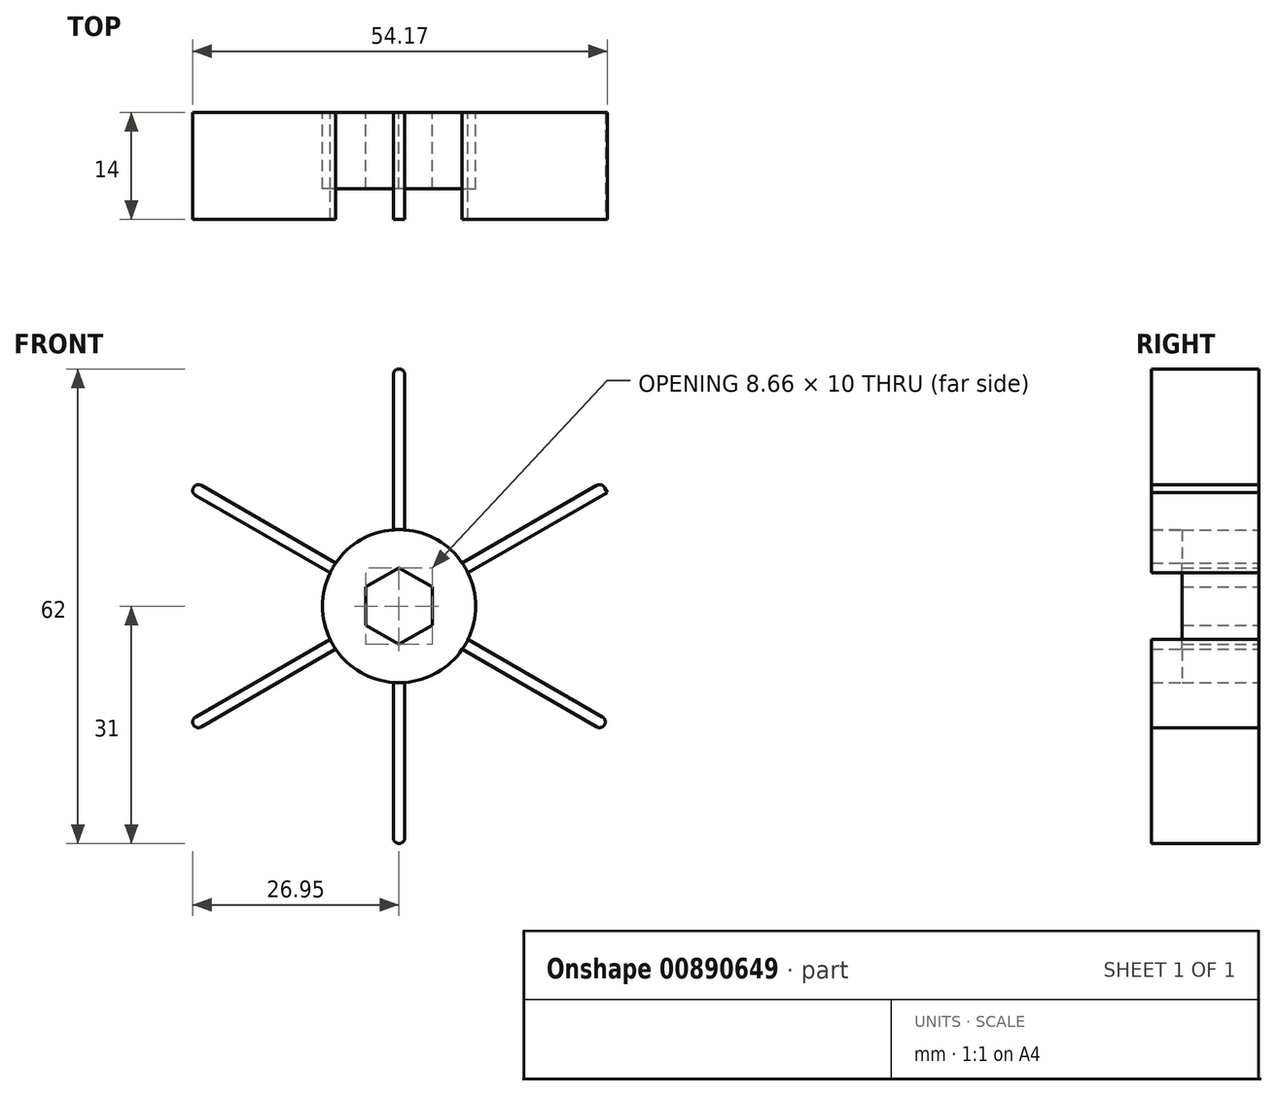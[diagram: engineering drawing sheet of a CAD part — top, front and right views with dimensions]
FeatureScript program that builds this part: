
annotation { "Feature Type Name" : "Feature", "Feature Type Description" : "" }
export const myFeature = defineFeature(function(context is Context, id is Id, definition is map)
    precondition{}
    {
        {
            var Q0;
            Q0=qCreatedBy(makeId("Front.planeOp"),FACE);
            var sketch = newSketch(context, id + "F0", { "sketchPlane" : qUnion([Q0])});
            skCircle(sketch, "E0", {"center": v(0, 0) * mm, "radius": 10 * mm});
            skCircle(sketch, "E1", {"center": v(0, 0) * mm, "radius": 5 * mm});
            skCircle(sketch, "E2.cCircle", {"center": v(0, 0) * mm, "radius": 5 * mm, "construction": true});
            skLineSegment(sketch, "E2.0", {"start": v(0, 5) * mm, "end": v(4.33, 2.5) * mm});
            skLineSegment(sketch, "E2.1", {"start": v(4.33, 2.5) * mm, "end": v(4.33, -2.5) * mm});
            skLineSegment(sketch, "E2.2", {"start": v(4.33, -2.5) * mm, "end": v(0, -5) * mm});
            skLineSegment(sketch, "E2.3", {"start": v(0, -5) * mm, "end": v(-4.33, -2.5) * mm});
            skLineSegment(sketch, "E2.4", {"start": v(-4.33, -2.5) * mm, "end": v(-4.33, 2.5) * mm});
            skLineSegment(sketch, "E2.5", {"start": v(-4.33, 2.5) * mm, "end": v(0, 5) * mm});
            skLineSegment(sketch, "E3", {"start": v(-0.75, 31) * mm, "end": v(0.75, 31) * mm});
            skLineSegment(sketch, "E4", {"start": v(0.75, 31) * mm, "end": v(0.75, 0) * mm});
            skLineSegment(sketch, "E5", {"start": v(-0.75, 31) * mm, "end": v(-0.75, 0) * mm});
            skLineSegment(sketch, "E6.1.0", {"start": v(-26.47, 16.15) * mm, "end": v(0.38, 0.65) * mm});
            skLineSegment(sketch, "E6.1.1", {"start": v(-27.22, 14.85) * mm, "end": v(-0.38, -0.65) * mm});
            skLineSegment(sketch, "E6.1.2", {"start": v(-27.22, 14.85) * mm, "end": v(-26.47, 16.15) * mm});
            skLineSegment(sketch, "E6.2.0", {"start": v(-27.22, -14.85) * mm, "end": v(-0.37, 0.65) * mm});
            skLineSegment(sketch, "E6.2.1", {"start": v(-26.47, -16.15) * mm, "end": v(0.38, -0.65) * mm});
            skLineSegment(sketch, "E6.2.2", {"start": v(-26.47, -16.15) * mm, "end": v(-27.22, -14.85) * mm});
            skLineSegment(sketch, "E6.3.0", {"start": v(-0.75, -31) * mm, "end": v(-0.75, 0) * mm});
            skLineSegment(sketch, "E6.3.1", {"start": v(0.75, -31) * mm, "end": v(0.75, 0) * mm});
            skLineSegment(sketch, "E6.3.2", {"start": v(0.75, -31) * mm, "end": v(-0.75, -31) * mm});
            skLineSegment(sketch, "E6.4.0", {"start": v(26.47, -16.15) * mm, "end": v(-0.38, -0.65) * mm});
            skLineSegment(sketch, "E6.4.1", {"start": v(27.22, -14.85) * mm, "end": v(0.38, 0.65) * mm});
            skLineSegment(sketch, "E6.4.2", {"start": v(27.22, -14.85) * mm, "end": v(26.47, -16.15) * mm});
            skLineSegment(sketch, "E6.5.0", {"start": v(27.22, 14.85) * mm, "end": v(0.38, -0.65) * mm});
            skLineSegment(sketch, "E6.5.1", {"start": v(26.47, 16.15) * mm, "end": v(-0.38, 0.65) * mm});
            skLineSegment(sketch, "E6.5.2", {"start": v(26.47, 16.15) * mm, "end": v(27.22, 14.85) * mm});
            skSolve(sketch);
        }
        {
            var Q0;
            {var subQ0=sQuery(id+"F0.wireOp",EDGE,"819567e6-a781-46ed-af89-72056181dca4.4.0");var subQ1=makeQuery(id+"F0.imprint","IMPRINT",VERTEX,{"derivedFrom":subQ0});Q0=makeQuery(id+"F0.imprint","IMPRINT",FACE,{"disambiguationData":[TD([[makeQuery(id+"F0.imprint","IMPRINT",EDGE,{"disambiguationData":[TD([[subQ1,1.0]])],"derivedFrom":subQ0}),1.0]])]});}
            var Q1;
            {var subQ2=sQuery(id+"F0.wireOp",EDGE,"819567e6-a781-46ed-af89-72056181dca4.5.0");var subQ4=makeQuery(id+"F0.imprint","IMPRINT",VERTEX,{"derivedFrom":subQ2});Q1=makeQuery(id+"F0.imprint","IMPRINT",FACE,{"disambiguationData":[TD([[makeQuery(id+"F0.imprint","IMPRINT",EDGE,{"disambiguationData":[TD([[subQ4,1.0]])],"derivedFrom":subQ2}),-1.0]])]});}
            var Q2;
            {var subQ5=sQuery(id+"F0.wireOp",EDGE,"819567e6-a781-46ed-af89-72056181dca4.5.0");var subQ6=makeQuery(id+"F0.imprint","IMPRINT",VERTEX,{"derivedFrom":subQ5});Q2=makeQuery(id+"F0.imprint","IMPRINT",FACE,{"disambiguationData":[TD([[makeQuery(id+"F0.imprint","IMPRINT",EDGE,{"disambiguationData":[TD([[subQ6,1.0]])],"derivedFrom":subQ5}),1.0]])]});}
            var Q3;
            {var subQ3=sQuery(id+"F0.wireOp",EDGE,"E0");var subQ10=sQuery(id+"F0.wireOp",EDGE,"98a826cf-b40a-42a3-8d70-f6cf4cde65dd2.MirrorCS");var subQ11=makeQuery(id+"F0.imprint","INTERSECT",VERTEX,{"derivedFrom":[subQ3,subQ10]});Q3=makeQuery(id+"F0.imprint","IMPRINT",FACE,{"disambiguationData":[TD([[makeQuery(id+"F0.imprint","IMPRINT",EDGE,{"disambiguationData":[TD([[subQ11,-1.0]])],"derivedFrom":subQ3}),1.0]])]});}
            var Q4;
            {var subQ3=sQuery(id+"F0.wireOp",EDGE,"E0");var subQ9=sQuery(id+"F0.wireOp",EDGE,"s4JnZFQR-gPvF-xN2i-koIt-LSXhCspGUzUX");var subQ11=makeQuery(id+"F0.imprint","INTERSECT",VERTEX,{"derivedFrom":[subQ3,subQ9]});Q4=makeQuery(id+"F0.imprint","IMPRINT",FACE,{"disambiguationData":[TD([[makeQuery(id+"F0.imprint","IMPRINT",EDGE,{"disambiguationData":[TD([[subQ11,-1.0]])],"derivedFrom":subQ3}),1.0]])]});}
            var Q5;
            {var subQ3=sQuery(id+"F0.wireOp",EDGE,"E0");var subQ6=sQuery(id+"F0.wireOp",EDGE,"819567e6-a781-46ed-af89-72056181dca4.1.2");var subQ12=makeQuery(id+"F0.imprint","INTERSECT",VERTEX,{"derivedFrom":[subQ3,subQ6]});Q5=makeQuery(id+"F0.imprint","IMPRINT",FACE,{"disambiguationData":[TD([[makeQuery(id+"F0.imprint","IMPRINT",EDGE,{"disambiguationData":[TD([[subQ12,-1.0]])],"derivedFrom":subQ3}),1.0]])]});}
            var Q6;
            {var subQ3=sQuery(id+"F0.wireOp",EDGE,"E0");var subQ6=sQuery(id+"F0.wireOp",EDGE,"819567e6-a781-46ed-af89-72056181dca4.1.0");var subQ8=makeQuery(id+"F0.imprint","INTERSECT",VERTEX,{"derivedFrom":[subQ3,subQ6]});Q6=makeQuery(id+"F0.imprint","IMPRINT",FACE,{"disambiguationData":[TD([[makeQuery(id+"F0.imprint","IMPRINT",EDGE,{"disambiguationData":[TD([[subQ8,-1.0]])],"derivedFrom":subQ3}),1.0]])]});}
            var Q7;
            {var subQ3=sQuery(id+"F0.wireOp",EDGE,"E0");var subQ10=sQuery(id+"F0.wireOp",EDGE,"819567e6-a781-46ed-af89-72056181dca4.2.2");var subQ12=makeQuery(id+"F0.imprint","INTERSECT",VERTEX,{"derivedFrom":[subQ3,subQ10]});Q7=makeQuery(id+"F0.imprint","IMPRINT",FACE,{"disambiguationData":[TD([[makeQuery(id+"F0.imprint","IMPRINT",EDGE,{"disambiguationData":[TD([[subQ12,-1.0]])],"derivedFrom":subQ3}),1.0]])]});}
            var Q8;
            {var subQ0=sQuery(id+"F0.wireOp",EDGE,"819567e6-a781-46ed-af89-72056181dca4.3.2");var subQ1=makeQuery(id+"F0.imprint","IMPRINT",VERTEX,{"derivedFrom":subQ0});Q8=makeQuery(id+"F0.imprint","IMPRINT",FACE,{"disambiguationData":[TD([[makeQuery(id+"F0.imprint","IMPRINT",EDGE,{"disambiguationData":[TD([[subQ1,1.0]])],"derivedFrom":subQ0}),-1.0]])]});}
            var Q9;
            {var subQ0=sQuery(id+"F0.wireOp",EDGE,"819567e6-a781-46ed-af89-72056181dca4.3.0");var subQ1=makeQuery(id+"F0.imprint","IMPRINT",VERTEX,{"derivedFrom":subQ0});Q9=makeQuery(id+"F0.imprint","IMPRINT",FACE,{"disambiguationData":[TD([[makeQuery(id+"F0.imprint","IMPRINT",EDGE,{"disambiguationData":[TD([[subQ1,1.0]])],"derivedFrom":subQ0}),-1.0]])]});}
            var Q10;
            {var subQ0=sQuery(id+"F0.wireOp",EDGE,"819567e6-a781-46ed-af89-72056181dca4.3.0");var subQ1=makeQuery(id+"F0.imprint","IMPRINT",VERTEX,{"derivedFrom":subQ0});Q10=makeQuery(id+"F0.imprint","IMPRINT",FACE,{"disambiguationData":[TD([[makeQuery(id+"F0.imprint","IMPRINT",EDGE,{"disambiguationData":[TD([[subQ1,1.0]])],"derivedFrom":subQ0}),1.0]])]});}
            var Q11;
            {var subQ0=sQuery(id+"F0.wireOp",EDGE,"819567e6-a781-46ed-af89-72056181dca4.4.0");var subQ1=makeQuery(id+"F0.imprint","IMPRINT",VERTEX,{"derivedFrom":subQ0});Q11=makeQuery(id+"F0.imprint","IMPRINT",FACE,{"disambiguationData":[TD([[makeQuery(id+"F0.imprint","IMPRINT",EDGE,{"disambiguationData":[TD([[subQ1,1.0]])],"derivedFrom":subQ0}),-1.0]])]});}
            var Q12;
            {var subQ0=sQuery(id+"F0.wireOp",EDGE,"819567e6-a781-46ed-af89-72056181dca4.5.2");var subQ1=sQuery(id+"F0.wireOp",EDGE,"E1");var subQ2=makeQuery(id+"F0.imprint","INTERSECT",VERTEX,{"disambiguationData":[OD(0.0)],"derivedFrom":[subQ1,subQ0]});Q12=makeQuery(id+"F0.imprint","IMPRINT",FACE,{"disambiguationData":[TD([[makeQuery(id+"F0.imprint","IMPRINT",EDGE,{"disambiguationData":[TD([[subQ2,1.0]])],"derivedFrom":subQ1}),1.0]])]});}
            var Q13;
            {var subQ1=sQuery(id+"F0.wireOp",EDGE,"E1");var subQ3=sQuery(id+"F0.wireOp",EDGE,"819567e6-a781-46ed-af89-72056181dca4.5.2");var subQ4=makeQuery(id+"F0.imprint","INTERSECT",VERTEX,{"disambiguationData":[OD(0.0)],"derivedFrom":[subQ1,subQ3]});Q13=makeQuery(id+"F0.imprint","IMPRINT",FACE,{"disambiguationData":[TD([[makeQuery(id+"F0.imprint","IMPRINT",EDGE,{"disambiguationData":[TD([[subQ4,1.0]])],"derivedFrom":subQ3}),1.0]])]});}
            var Q14;
            {var subQ1=sQuery(id+"F0.wireOp",EDGE,"E1");var subQ3=sQuery(id+"F0.wireOp",EDGE,"819567e6-a781-46ed-af89-72056181dca4.4.0");var subQ4=makeQuery(id+"F0.imprint","INTERSECT",VERTEX,{"disambiguationData":[OD(1.0)],"derivedFrom":[subQ1,subQ3]});Q14=makeQuery(id+"F0.imprint","IMPRINT",FACE,{"disambiguationData":[TD([[makeQuery(id+"F0.imprint","IMPRINT",EDGE,{"disambiguationData":[TD([[subQ4,1.0]])],"derivedFrom":subQ3}),-1.0]])]});}
            var Q15;
            {var subQ1=sQuery(id+"F0.wireOp",EDGE,"E1");var subQ3=sQuery(id+"F0.wireOp",EDGE,"819567e6-a781-46ed-af89-72056181dca4.4.2");var subQ4=makeQuery(id+"F0.imprint","INTERSECT",VERTEX,{"disambiguationData":[OD(1.0)],"derivedFrom":[subQ1,subQ3]});Q15=makeQuery(id+"F0.imprint","IMPRINT",FACE,{"disambiguationData":[TD([[makeQuery(id+"F0.imprint","IMPRINT",EDGE,{"disambiguationData":[TD([[subQ4,1.0]])],"derivedFrom":subQ3}),1.0]])]});}
            var Q16;
            {var subQ0=sQuery(id+"F0.wireOp",EDGE,"819567e6-a781-46ed-af89-72056181dca4.3.0");var subQ1=sQuery(id+"F0.wireOp",EDGE,"E1");var subQ2=makeQuery(id+"F0.imprint","INTERSECT",VERTEX,{"disambiguationData":[OD(1.0)],"derivedFrom":[subQ1,subQ0]});Q16=makeQuery(id+"F0.imprint","IMPRINT",FACE,{"disambiguationData":[TD([[makeQuery(id+"F0.imprint","IMPRINT",EDGE,{"disambiguationData":[TD([[subQ2,-1.0]])],"derivedFrom":subQ1}),1.0]])]});}
            var Q17;
            {var subQ1=sQuery(id+"F0.wireOp",EDGE,"E1");var subQ3=sQuery(id+"F0.wireOp",EDGE,"819567e6-a781-46ed-af89-72056181dca4.3.0");var subQ4=makeQuery(id+"F0.imprint","INTERSECT",VERTEX,{"disambiguationData":[OD(1.0)],"derivedFrom":[subQ1,subQ3]});Q17=makeQuery(id+"F0.imprint","IMPRINT",FACE,{"disambiguationData":[TD([[makeQuery(id+"F0.imprint","IMPRINT",EDGE,{"disambiguationData":[TD([[subQ4,1.0]])],"derivedFrom":subQ3}),-1.0]])]});}
            var Q18;
            {var subQ0=sQuery(id+"F0.wireOp",EDGE,"819567e6-a781-46ed-af89-72056181dca4.5.2");var subQ1=sQuery(id+"F0.wireOp",EDGE,"E1");var subQ2=makeQuery(id+"F0.imprint","INTERSECT",VERTEX,{"disambiguationData":[OD(1.0)],"derivedFrom":[subQ1,subQ0]});Q18=makeQuery(id+"F0.imprint","IMPRINT",FACE,{"disambiguationData":[TD([[makeQuery(id+"F0.imprint","IMPRINT",EDGE,{"disambiguationData":[TD([[subQ2,-1.0]])],"derivedFrom":subQ1}),1.0]])]});}
            var Q19;
            {var subQ1=sQuery(id+"F0.wireOp",EDGE,"E1");var subQ3=sQuery(id+"F0.wireOp",EDGE,"819567e6-a781-46ed-af89-72056181dca4.3.2");var subQ4=makeQuery(id+"F0.imprint","INTERSECT",VERTEX,{"disambiguationData":[OD(1.0)],"derivedFrom":[subQ1,subQ3]});Q19=makeQuery(id+"F0.imprint","IMPRINT",FACE,{"disambiguationData":[TD([[makeQuery(id+"F0.imprint","IMPRINT",EDGE,{"disambiguationData":[TD([[subQ4,1.0]])],"derivedFrom":subQ3}),1.0]])]});}
            var Q20;
            {var subQ1=sQuery(id+"F0.wireOp",EDGE,"E1");var subQ3=sQuery(id+"F0.wireOp",EDGE,"819567e6-a781-46ed-af89-72056181dca4.5.2");var subQ4=makeQuery(id+"F0.imprint","INTERSECT",VERTEX,{"disambiguationData":[OD(1.0)],"derivedFrom":[subQ1,subQ3]});Q20=makeQuery(id+"F0.imprint","IMPRINT",FACE,{"disambiguationData":[TD([[makeQuery(id+"F0.imprint","IMPRINT",EDGE,{"disambiguationData":[TD([[subQ4,-1.0]])],"derivedFrom":subQ3}),1.0]])]});}
            var Q21;
            {var subQ0=sQuery(id+"F0.wireOp",EDGE,"819567e6-a781-46ed-af89-72056181dca4.4.2");var subQ1=sQuery(id+"F0.wireOp",EDGE,"E1");var subQ2=makeQuery(id+"F0.imprint","INTERSECT",VERTEX,{"disambiguationData":[OD(0.0)],"derivedFrom":[subQ1,subQ0]});Q21=makeQuery(id+"F0.imprint","IMPRINT",FACE,{"disambiguationData":[TD([[makeQuery(id+"F0.imprint","IMPRINT",EDGE,{"disambiguationData":[TD([[subQ2,-1.0]])],"derivedFrom":subQ1}),1.0]])]});}
            var Q22;
            {var subQ1=sQuery(id+"F0.wireOp",EDGE,"E1");var subQ3=sQuery(id+"F0.wireOp",EDGE,"819567e6-a781-46ed-af89-72056181dca4.5.0");var subQ4=makeQuery(id+"F0.imprint","INTERSECT",VERTEX,{"disambiguationData":[OD(1.0)],"derivedFrom":[subQ1,subQ3]});Q22=makeQuery(id+"F0.imprint","IMPRINT",FACE,{"disambiguationData":[TD([[makeQuery(id+"F0.imprint","IMPRINT",EDGE,{"disambiguationData":[TD([[subQ4,-1.0]])],"derivedFrom":subQ3}),-1.0]])]});}
            var Q23;
            {var subQ1=sQuery(id+"F0.wireOp",EDGE,"E1");var subQ3=sQuery(id+"F0.wireOp",EDGE,"819567e6-a781-46ed-af89-72056181dca4.4.2");var subQ4=makeQuery(id+"F0.imprint","INTERSECT",VERTEX,{"disambiguationData":[OD(0.0)],"derivedFrom":[subQ1,subQ3]});Q23=makeQuery(id+"F0.imprint","IMPRINT",FACE,{"disambiguationData":[TD([[makeQuery(id+"F0.imprint","IMPRINT",EDGE,{"disambiguationData":[TD([[subQ4,-1.0]])],"derivedFrom":subQ3}),1.0]])]});}
            var Q24;
            {var subQ1=sQuery(id+"F0.wireOp",EDGE,"E1");var subQ3=sQuery(id+"F0.wireOp",EDGE,"819567e6-a781-46ed-af89-72056181dca4.4.0");var subQ4=makeQuery(id+"F0.imprint","INTERSECT",VERTEX,{"disambiguationData":[OD(0.0)],"derivedFrom":[subQ1,subQ3]});Q24=makeQuery(id+"F0.imprint","IMPRINT",FACE,{"disambiguationData":[TD([[makeQuery(id+"F0.imprint","IMPRINT",EDGE,{"disambiguationData":[TD([[subQ4,-1.0]])],"derivedFrom":subQ3}),-1.0]])]});}
            var Q25;
            {var subQ0=sQuery(id+"F0.wireOp",EDGE,"819567e6-a781-46ed-af89-72056181dca4.3.2");var subQ1=sQuery(id+"F0.wireOp",EDGE,"E1");var subQ2=makeQuery(id+"F0.imprint","INTERSECT",VERTEX,{"disambiguationData":[OD(0.0)],"derivedFrom":[subQ1,subQ0]});Q25=makeQuery(id+"F0.imprint","IMPRINT",FACE,{"disambiguationData":[TD([[makeQuery(id+"F0.imprint","IMPRINT",EDGE,{"disambiguationData":[TD([[subQ2,-1.0]])],"derivedFrom":subQ1}),1.0]])]});}
            var Q26;
            {var subQ1=sQuery(id+"F0.wireOp",EDGE,"E1");var subQ3=sQuery(id+"F0.wireOp",EDGE,"819567e6-a781-46ed-af89-72056181dca4.3.2");var subQ4=makeQuery(id+"F0.imprint","INTERSECT",VERTEX,{"disambiguationData":[OD(0.0)],"derivedFrom":[subQ1,subQ3]});Q26=makeQuery(id+"F0.imprint","IMPRINT",FACE,{"disambiguationData":[TD([[makeQuery(id+"F0.imprint","IMPRINT",EDGE,{"disambiguationData":[TD([[subQ4,-1.0]])],"derivedFrom":subQ3}),1.0]])]});}
            var Q27;
            {var subQ1=sQuery(id+"F0.wireOp",EDGE,"E1");var subQ3=sQuery(id+"F0.wireOp",EDGE,"819567e6-a781-46ed-af89-72056181dca4.3.0");var subQ4=makeQuery(id+"F0.imprint","INTERSECT",VERTEX,{"disambiguationData":[OD(0.0)],"derivedFrom":[subQ1,subQ3]});Q27=makeQuery(id+"F0.imprint","IMPRINT",FACE,{"disambiguationData":[TD([[makeQuery(id+"F0.imprint","IMPRINT",EDGE,{"disambiguationData":[TD([[subQ4,-1.0]])],"derivedFrom":subQ3}),-1.0]])]});}
            var Q28;
            {var subQ0=sQuery(id+"F0.wireOp",EDGE,"819567e6-a781-46ed-af89-72056181dca4.5.0");var subQ1=sQuery(id+"F0.wireOp",EDGE,"E1");var subQ2=makeQuery(id+"F0.imprint","INTERSECT",VERTEX,{"disambiguationData":[OD(0.0)],"derivedFrom":[subQ1,subQ0]});Q28=makeQuery(id+"F0.imprint","IMPRINT",FACE,{"disambiguationData":[TD([[makeQuery(id+"F0.imprint","IMPRINT",EDGE,{"disambiguationData":[TD([[subQ2,-1.0]])],"derivedFrom":subQ1}),1.0]])]});}
            var Q29;
            {var subQ1=sQuery(id+"F0.wireOp",EDGE,"E1");var subQ3=sQuery(id+"F0.wireOp",EDGE,"819567e6-a781-46ed-af89-72056181dca4.5.0");var subQ4=makeQuery(id+"F0.imprint","INTERSECT",VERTEX,{"disambiguationData":[OD(0.0)],"derivedFrom":[subQ1,subQ3]});Q29=makeQuery(id+"F0.imprint","IMPRINT",FACE,{"disambiguationData":[TD([[makeQuery(id+"F0.imprint","IMPRINT",EDGE,{"disambiguationData":[TD([[subQ4,1.0]])],"derivedFrom":subQ3}),-1.0]])]});}
            var Q30;
            {var subQ1=sQuery(id+"F0.wireOp",EDGE,"E0");var subQ6=sQuery(id+"F0.wireOp",EDGE,"E6.5.1");var subQ8=makeQuery(id+"F0.imprint","INTERSECT",VERTEX,{"derivedFrom":[subQ1,subQ6]});Q30=makeQuery(id+"F0.imprint","IMPRINT",FACE,{"disambiguationData":[TD([[makeQuery(id+"F0.imprint","IMPRINT",EDGE,{"disambiguationData":[TD([[subQ8,1.0]])],"derivedFrom":subQ1}),1.0]])]});}
            var Q31;
            {var subQ4=sQuery(id+"F0.wireOp",EDGE,"E4");var subQ5=sQuery(id+"F0.wireOp",EDGE,"E0");var subQ6=makeQuery(id+"F0.imprint","INTERSECT",VERTEX,{"derivedFrom":[subQ5,subQ4]});Q31=makeQuery(id+"F0.imprint","IMPRINT",FACE,{"disambiguationData":[TD([[makeQuery(id+"F0.imprint","IMPRINT",EDGE,{"disambiguationData":[TD([[subQ6,-1.0]])],"derivedFrom":subQ5}),1.0]])]});}
            var Q32;
            {var subQ0=sQuery(id+"F0.wireOp",EDGE,"E6.1.0");var subQ1=sQuery(id+"F0.wireOp",EDGE,"E0");var subQ2=makeQuery(id+"F0.imprint","INTERSECT",VERTEX,{"derivedFrom":[subQ1,subQ0]});Q32=makeQuery(id+"F0.imprint","IMPRINT",FACE,{"disambiguationData":[TD([[makeQuery(id+"F0.imprint","IMPRINT",EDGE,{"disambiguationData":[TD([[subQ2,-1.0]])],"derivedFrom":subQ1}),1.0]])]});}
            var Q33;
            {var subQ0=sQuery(id+"F0.wireOp",EDGE,"E6.2.0");var subQ1=sQuery(id+"F0.wireOp",EDGE,"E0");var subQ2=makeQuery(id+"F0.imprint","INTERSECT",VERTEX,{"derivedFrom":[subQ1,subQ0]});Q33=makeQuery(id+"F0.imprint","IMPRINT",FACE,{"disambiguationData":[TD([[makeQuery(id+"F0.imprint","IMPRINT",EDGE,{"disambiguationData":[TD([[subQ2,-1.0]])],"derivedFrom":subQ1}),1.0]])]});}
            var Q34;
            {var subQ4=sQuery(id+"F0.wireOp",EDGE,"E6.3.0");var subQ6=sQuery(id+"F0.wireOp",EDGE,"E0");var subQ7=makeQuery(id+"F0.imprint","INTERSECT",VERTEX,{"derivedFrom":[subQ6,subQ4]});Q34=makeQuery(id+"F0.imprint","IMPRINT",FACE,{"disambiguationData":[TD([[makeQuery(id+"F0.imprint","IMPRINT",EDGE,{"disambiguationData":[TD([[subQ7,-1.0]])],"derivedFrom":subQ6}),1.0]])]});}
            var Q35;
            {var subQ0=sQuery(id+"F0.wireOp",EDGE,"E6.4.0");var subQ1=sQuery(id+"F0.wireOp",EDGE,"E0");var subQ2=makeQuery(id+"F0.imprint","INTERSECT",VERTEX,{"derivedFrom":[subQ1,subQ0]});Q35=makeQuery(id+"F0.imprint","IMPRINT",FACE,{"disambiguationData":[TD([[makeQuery(id+"F0.imprint","IMPRINT",EDGE,{"disambiguationData":[TD([[subQ2,-1.0]])],"derivedFrom":subQ1}),1.0]])]});}
            var Q36;
            {var subQ0=sQuery(id+"F0.wireOp",EDGE,"E6.5.1");var subQ1=sQuery(id+"F0.wireOp",EDGE,"E1");var subQ2=makeQuery(id+"F0.imprint","INTERSECT",VERTEX,{"derivedFrom":[subQ1,subQ0]});Q36=makeQuery(id+"F0.imprint","IMPRINT",FACE,{"disambiguationData":[TD([[makeQuery(id+"F0.imprint","IMPRINT",EDGE,{"disambiguationData":[TD([[subQ2,-1.0]])],"derivedFrom":subQ1}),1.0]])]});}
            var Q37;
            {var subQ0=sQuery(id+"F0.wireOp",EDGE,"E6.5.0");var subQ1=sQuery(id+"F0.wireOp",EDGE,"E1");var subQ2=makeQuery(id+"F0.imprint","INTERSECT",VERTEX,{"derivedFrom":[subQ1,subQ0]});Q37=makeQuery(id+"F0.imprint","IMPRINT",FACE,{"disambiguationData":[TD([[makeQuery(id+"F0.imprint","IMPRINT",EDGE,{"disambiguationData":[TD([[subQ2,1.0]])],"derivedFrom":subQ1}),1.0]])]});}
            var Q38;
            {var subQ0=sQuery(id+"F0.wireOp",EDGE,"E6.3.1");var subQ1=sQuery(id+"F0.wireOp",EDGE,"E1");var subQ2=makeQuery(id+"F0.imprint","INTERSECT",VERTEX,{"derivedFrom":[subQ1,subQ0]});Q38=makeQuery(id+"F0.imprint","IMPRINT",FACE,{"disambiguationData":[TD([[makeQuery(id+"F0.imprint","IMPRINT",EDGE,{"disambiguationData":[TD([[subQ2,-1.0]])],"derivedFrom":subQ1}),1.0]])]});}
            var Q39;
            {var subQ0=sQuery(id+"F0.wireOp",EDGE,"E6.2.1");var subQ1=sQuery(id+"F0.wireOp",EDGE,"E1");var subQ2=makeQuery(id+"F0.imprint","INTERSECT",VERTEX,{"derivedFrom":[subQ1,subQ0]});Q39=makeQuery(id+"F0.imprint","IMPRINT",FACE,{"disambiguationData":[TD([[makeQuery(id+"F0.imprint","IMPRINT",EDGE,{"disambiguationData":[TD([[subQ2,-1.0]])],"derivedFrom":subQ1}),1.0]])]});}
            var Q40;
            {var subQ0=sQuery(id+"F0.wireOp",EDGE,"E6.1.1");var subQ1=sQuery(id+"F0.wireOp",EDGE,"E1");var subQ2=makeQuery(id+"F0.imprint","INTERSECT",VERTEX,{"derivedFrom":[subQ1,subQ0]});Q40=makeQuery(id+"F0.imprint","IMPRINT",FACE,{"disambiguationData":[TD([[makeQuery(id+"F0.imprint","IMPRINT",EDGE,{"disambiguationData":[TD([[subQ2,-1.0]])],"derivedFrom":subQ1}),1.0]])]});}
            var Q41;
            {var subQ0=sQuery(id+"F0.wireOp",EDGE,"E5");var subQ1=sQuery(id+"F0.wireOp",EDGE,"E1");var subQ2=makeQuery(id+"F0.imprint","INTERSECT",VERTEX,{"derivedFrom":[subQ1,subQ0]});Q41=makeQuery(id+"F0.imprint","IMPRINT",FACE,{"disambiguationData":[TD([[makeQuery(id+"F0.imprint","IMPRINT",EDGE,{"disambiguationData":[TD([[subQ2,-1.0]])],"derivedFrom":subQ1}),1.0]])]});}
            extrude(context, id + "F1", {"entities" : qUnion([Q0, Q1, Q2, Q3, Q4, Q5, Q6, Q7, Q8, Q9, Q10, Q11, Q12, Q13, Q14, Q15, Q16, Q17, Q18, Q19, Q20, Q21, Q22, Q23, Q24, Q25, Q26, Q27, Q28, Q29, Q30, Q31, Q32, Q33, Q34, Q35, Q36, Q37, Q38, Q39, Q40, Q41]), "depth" : 10 * mm, "offsetDistance" : 25 * mm});
        }
        {
            var Q0;
            {var subQ5=sQuery(id+"F0.wireOp",EDGE,"E3");Q0=makeQuery(id+"F0.imprint","IMPRINT",FACE,{"disambiguationData":[TD([[makeQuery(id+"F0.imprint","IMPRINT",EDGE,{"derivedFrom":subQ5}),-1.0]])]});}
            var Q1;
            {var subQ5=sQuery(id+"F0.wireOp",EDGE,"819567e6-a781-46ed-af89-72056181dca4.5.1");Q1=makeQuery(id+"F0.imprint","IMPRINT",FACE,{"disambiguationData":[TD([[makeQuery(id+"F0.imprint","IMPRINT",EDGE,{"derivedFrom":subQ5}),-1.0]])]});}
            var Q2;
            {var subQ5=sQuery(id+"F0.wireOp",EDGE,"819567e6-a781-46ed-af89-72056181dca4.4.1");Q2=makeQuery(id+"F0.imprint","IMPRINT",FACE,{"disambiguationData":[TD([[makeQuery(id+"F0.imprint","IMPRINT",EDGE,{"derivedFrom":subQ5}),-1.0]])]});}
            var Q3;
            {var subQ5=sQuery(id+"F0.wireOp",EDGE,"819567e6-a781-46ed-af89-72056181dca4.3.1");Q3=makeQuery(id+"F0.imprint","IMPRINT",FACE,{"disambiguationData":[TD([[makeQuery(id+"F0.imprint","IMPRINT",EDGE,{"derivedFrom":subQ5}),-1.0]])]});}
            var Q4;
            {var subQ5=sQuery(id+"F0.wireOp",EDGE,"819567e6-a781-46ed-af89-72056181dca4.2.1");Q4=makeQuery(id+"F0.imprint","IMPRINT",FACE,{"disambiguationData":[TD([[makeQuery(id+"F0.imprint","IMPRINT",EDGE,{"derivedFrom":subQ5}),-1.0]])]});}
            var Q5;
            {var subQ5=sQuery(id+"F0.wireOp",EDGE,"819567e6-a781-46ed-af89-72056181dca4.1.1");Q5=makeQuery(id+"F0.imprint","IMPRINT",FACE,{"disambiguationData":[TD([[makeQuery(id+"F0.imprint","IMPRINT",EDGE,{"derivedFrom":subQ5}),-1.0]])]});}
            var Q6;
            {var subQ5=sQuery(id+"F0.wireOp",EDGE,"E6.4.2");Q6=makeQuery(id+"F0.imprint","IMPRINT",FACE,{"disambiguationData":[TD([[makeQuery(id+"F0.imprint","IMPRINT",EDGE,{"derivedFrom":subQ5}),-1.0]])]});}
            var Q7;
            {var subQ5=sQuery(id+"F0.wireOp",EDGE,"E6.5.2");Q7=makeQuery(id+"F0.imprint","IMPRINT",FACE,{"disambiguationData":[TD([[makeQuery(id+"F0.imprint","IMPRINT",EDGE,{"derivedFrom":subQ5}),-1.0]])]});}
            var Q8;
            {var subQ5=sQuery(id+"F0.wireOp",EDGE,"E6.3.2");Q8=makeQuery(id+"F0.imprint","IMPRINT",FACE,{"disambiguationData":[TD([[makeQuery(id+"F0.imprint","IMPRINT",EDGE,{"derivedFrom":subQ5}),-1.0]])]});}
            var Q9;
            {var subQ5=sQuery(id+"F0.wireOp",EDGE,"E6.2.2");Q9=makeQuery(id+"F0.imprint","IMPRINT",FACE,{"disambiguationData":[TD([[makeQuery(id+"F0.imprint","IMPRINT",EDGE,{"derivedFrom":subQ5}),-1.0]])]});}
            var Q10;
            {var subQ5=sQuery(id+"F0.wireOp",EDGE,"E6.1.2");Q10=makeQuery(id+"F0.imprint","IMPRINT",FACE,{"disambiguationData":[TD([[makeQuery(id+"F0.imprint","IMPRINT",EDGE,{"derivedFrom":subQ5}),-1.0]])]});}
            extrude(context, id + "F2", {"entities" : qUnion([Q0, Q1, Q2, Q3, Q4, Q5, Q6, Q7, Q8, Q9, Q10]), "operationType" : NewBodyOperationType.ADD, "depth" : 14 * mm, "offsetDistance" : 25 * mm});
        }
        {
            var Q0;
            Q0=makeQuery(id+"F2.opExtrude","SWEPT_EDGE",EDGE,{"disambiguationData":[OSD([sQuery(id+"F0.wireOp",EDGE,"98a826cf-b40a-42a3-8d70-f6cf4cde65dd2.MirrorCS"),sQuery(id+"F0.wireOp",EDGE,"E3")])]});
            var Q1;
            Q1=makeQuery(id+"F2.opExtrude","SWEPT_EDGE",EDGE,{"disambiguationData":[OSD([sQuery(id+"F0.wireOp",EDGE,"s4JnZFQR-gPvF-xN2i-koIt-LSXhCspGUzUX"),sQuery(id+"F0.wireOp",EDGE,"E3")])]});
            var Q2;
            Q2=makeQuery(id+"F2.opExtrude","SWEPT_EDGE",EDGE,{"disambiguationData":[OSD([sQuery(id+"F0.wireOp",EDGE,"819567e6-a781-46ed-af89-72056181dca4.5.0"),sQuery(id+"F0.wireOp",EDGE,"819567e6-a781-46ed-af89-72056181dca4.5.1")])]});
            var Q3;
            Q3=makeQuery(id+"F2.opExtrude","SWEPT_EDGE",EDGE,{"disambiguationData":[OSD([sQuery(id+"F0.wireOp",EDGE,"819567e6-a781-46ed-af89-72056181dca4.5.1"),sQuery(id+"F0.wireOp",EDGE,"819567e6-a781-46ed-af89-72056181dca4.5.2")])]});
            var Q4;
            Q4=makeQuery(id+"F2.opExtrude","SWEPT_EDGE",EDGE,{"disambiguationData":[OSD([sQuery(id+"F0.wireOp",EDGE,"819567e6-a781-46ed-af89-72056181dca4.4.0"),sQuery(id+"F0.wireOp",EDGE,"819567e6-a781-46ed-af89-72056181dca4.4.1")])]});
            var Q5;
            Q5=makeQuery(id+"F2.opExtrude","SWEPT_EDGE",EDGE,{"disambiguationData":[OSD([sQuery(id+"F0.wireOp",EDGE,"819567e6-a781-46ed-af89-72056181dca4.4.1"),sQuery(id+"F0.wireOp",EDGE,"819567e6-a781-46ed-af89-72056181dca4.4.2")])]});
            var Q6;
            Q6=makeQuery(id+"F2.opExtrude","SWEPT_EDGE",EDGE,{"disambiguationData":[OSD([sQuery(id+"F0.wireOp",EDGE,"819567e6-a781-46ed-af89-72056181dca4.3.0"),sQuery(id+"F0.wireOp",EDGE,"819567e6-a781-46ed-af89-72056181dca4.3.1")])]});
            var Q7;
            Q7=makeQuery(id+"F2.opExtrude","SWEPT_EDGE",EDGE,{"disambiguationData":[OSD([sQuery(id+"F0.wireOp",EDGE,"819567e6-a781-46ed-af89-72056181dca4.3.1"),sQuery(id+"F0.wireOp",EDGE,"819567e6-a781-46ed-af89-72056181dca4.3.2")])]});
            var Q8;
            Q8=makeQuery(id+"F2.opExtrude","SWEPT_EDGE",EDGE,{"disambiguationData":[OSD([sQuery(id+"F0.wireOp",EDGE,"819567e6-a781-46ed-af89-72056181dca4.1.1"),sQuery(id+"F0.wireOp",EDGE,"819567e6-a781-46ed-af89-72056181dca4.1.2")])]});
            var Q9;
            Q9=makeQuery(id+"F2.opExtrude","SWEPT_EDGE",EDGE,{"disambiguationData":[OSD([sQuery(id+"F0.wireOp",EDGE,"819567e6-a781-46ed-af89-72056181dca4.1.0"),sQuery(id+"F0.wireOp",EDGE,"819567e6-a781-46ed-af89-72056181dca4.1.1")])]});
            var Q10;
            Q10=makeQuery(id+"F2.opExtrude","SWEPT_EDGE",EDGE,{"disambiguationData":[OSD([sQuery(id+"F0.wireOp",EDGE,"819567e6-a781-46ed-af89-72056181dca4.2.1"),sQuery(id+"F0.wireOp",EDGE,"819567e6-a781-46ed-af89-72056181dca4.2.2")])]});
            var Q11;
            Q11=makeQuery(id+"F2.opExtrude","SWEPT_EDGE",EDGE,{"disambiguationData":[OSD([sQuery(id+"F0.wireOp",EDGE,"819567e6-a781-46ed-af89-72056181dca4.2.0"),sQuery(id+"F0.wireOp",EDGE,"819567e6-a781-46ed-af89-72056181dca4.2.1")])]});
            var Q12;
            Q12=makeQuery(id+"F2.opExtrude","SWEPT_EDGE",EDGE,{"disambiguationData":[OSD([sQuery(id+"F0.wireOp",EDGE,"E6.5.1"),sQuery(id+"F0.wireOp",EDGE,"E6.5.2")])]});
            var Q13;
            Q13=makeQuery(id+"F2.opExtrude","SWEPT_EDGE",EDGE,{"disambiguationData":[OSD([sQuery(id+"F0.wireOp",EDGE,"E6.4.1"),sQuery(id+"F0.wireOp",EDGE,"E6.4.2")])]});
            var Q14;
            Q14=makeQuery(id+"F2.opExtrude","SWEPT_EDGE",EDGE,{"disambiguationData":[OSD([sQuery(id+"F0.wireOp",EDGE,"E6.4.0"),sQuery(id+"F0.wireOp",EDGE,"E6.4.2")])]});
            var Q15;
            Q15=makeQuery(id+"F2.opExtrude","SWEPT_EDGE",EDGE,{"disambiguationData":[OSD([sQuery(id+"F0.wireOp",EDGE,"E6.3.1"),sQuery(id+"F0.wireOp",EDGE,"E6.3.2")])]});
            var Q16;
            Q16=makeQuery(id+"F2.opExtrude","SWEPT_EDGE",EDGE,{"disambiguationData":[OSD([sQuery(id+"F0.wireOp",EDGE,"E6.3.0"),sQuery(id+"F0.wireOp",EDGE,"E6.3.2")])]});
            var Q17;
            Q17=makeQuery(id+"F2.opExtrude","SWEPT_EDGE",EDGE,{"disambiguationData":[OSD([sQuery(id+"F0.wireOp",EDGE,"E6.2.1"),sQuery(id+"F0.wireOp",EDGE,"E6.2.2")])]});
            var Q18;
            Q18=makeQuery(id+"F2.opExtrude","SWEPT_EDGE",EDGE,{"disambiguationData":[OSD([sQuery(id+"F0.wireOp",EDGE,"E6.2.0"),sQuery(id+"F0.wireOp",EDGE,"E6.2.2")])]});
            var Q19;
            Q19=makeQuery(id+"F2.opExtrude","SWEPT_EDGE",EDGE,{"disambiguationData":[OSD([sQuery(id+"F0.wireOp",EDGE,"E6.1.0"),sQuery(id+"F0.wireOp",EDGE,"E6.1.2")])]});
            var Q20;
            Q20=makeQuery(id+"F2.opExtrude","SWEPT_EDGE",EDGE,{"disambiguationData":[OSD([sQuery(id+"F0.wireOp",EDGE,"E6.1.1"),sQuery(id+"F0.wireOp",EDGE,"E6.1.2")])]});
            fillet(context, id + "F3", {"entities" : qUnion([Q0, Q1, Q2, Q3, Q4, Q5, Q6, Q7, Q8, Q9, Q10, Q11, Q12, Q13, Q14, Q15, Q16, Q17, Q18, Q19, Q20]), "radius" : 0.75 * mm, "tangentPropagation" : true, "allowEdgeOverflow" : false});
        }
    });
